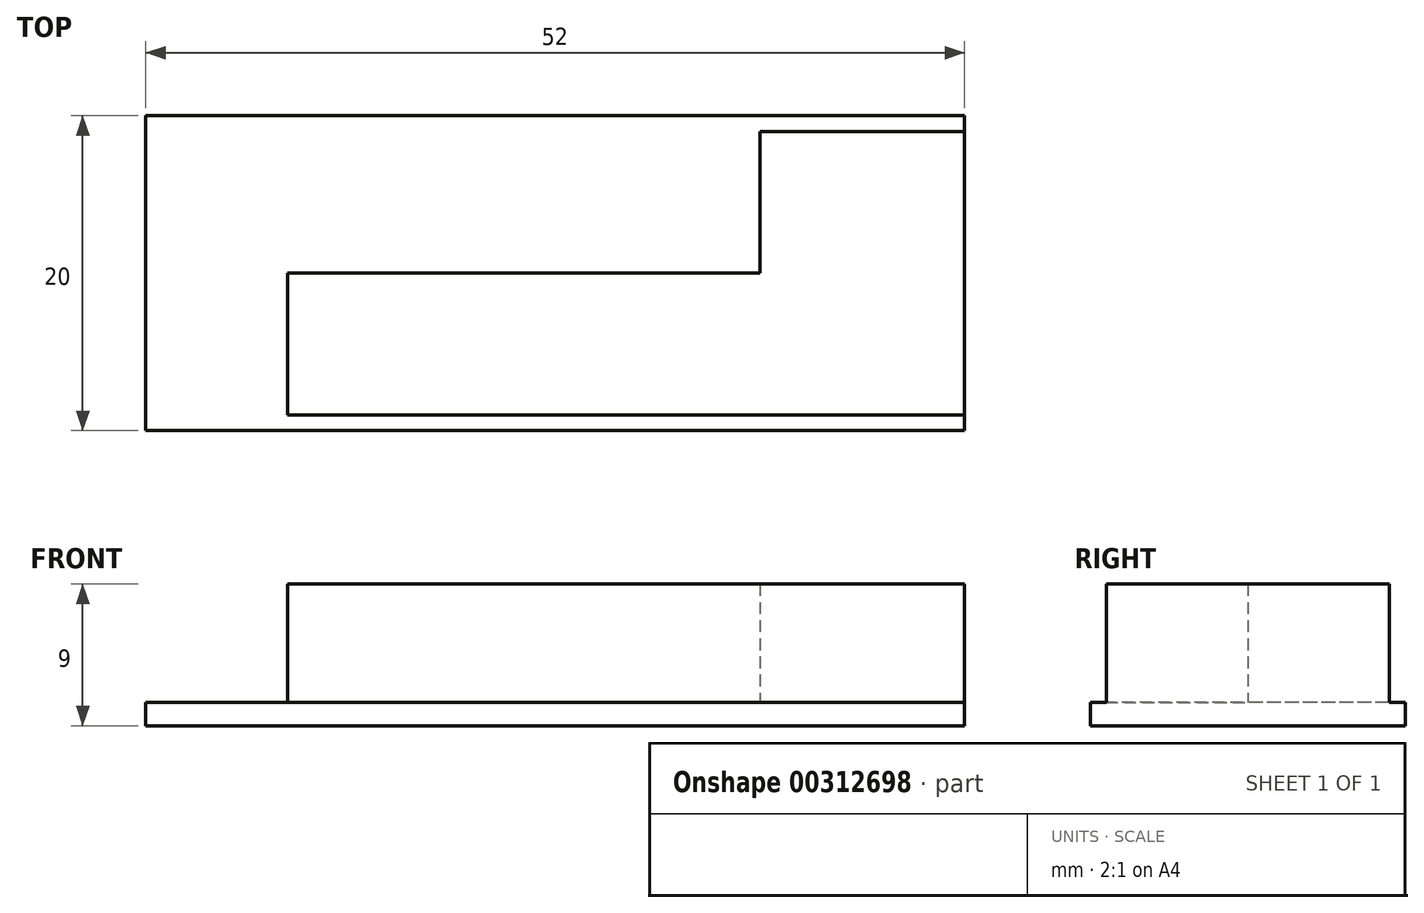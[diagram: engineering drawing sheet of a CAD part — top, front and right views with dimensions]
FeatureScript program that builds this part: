
annotation { "Feature Type Name" : "Feature", "Feature Type Description" : "" }
export const myFeature = defineFeature(function(context is Context, id is Id, definition is map)
    precondition{}
    {
        {
            var Q0;
            Q0=qCreatedBy(makeId("Top.planeOp"),FACE);
            var sketch = newSketch(context, id + "F0", { "sketchPlane" : qUnion([Q0])});
            skLineSegment(sketch, "E0.bottom", {"start": v(0, 0) * mm, "end": v(52, 0) * mm});
            skLineSegment(sketch, "E0.top", {"start": v(0, -20) * mm, "end": v(52, -20) * mm});
            skLineSegment(sketch, "E0.left", {"start": v(0, 0) * mm, "end": v(0, -20) * mm});
            skLineSegment(sketch, "E0.right", {"start": v(52, 0) * mm, "end": v(52, -20) * mm});
            skSolve(sketch);
        }
        {
            var Q0;
            Q0=makeQuery(id+"F0.imprint","IMPRINT",FACE,{"disambiguationData":[TD([[makeQuery(id+"F0.imprint","IMPRINT",EDGE,{"derivedFrom":sQuery(id+"F0.wireOp",EDGE,"E0.bottom")}),-1.0]])]});
            extrude(context, id + "F1", {"entities" : qUnion([Q0]), "depth" : 1.5 * mm});
        }
        {
            var Q0;
            Q0=makeQuery(id+"F1.opExtrude","CAP_FACE",FACE,{"disambiguationData":[OSD([sQuery(id+"F0.wireOp",EDGE,"E0.bottom"),sQuery(id+"F0.wireOp",EDGE,"E0.top"),sQuery(id+"F0.wireOp",EDGE,"E0.left"),sQuery(id+"F0.wireOp",EDGE,"E0.right")])],"isStart":false});
            var sketch = newSketch(context, id + "F2", { "sketchPlane" : qUnion([Q0])});
            skLineSegment(sketch, "E1.bottom", {"start": v(52, -1) * mm, "end": v(39, -1) * mm});
            skLineSegment(sketch, "E1.top", {"start": v(52, -19) * mm, "end": v(39, -19) * mm});
            skLineSegment(sketch, "E1.left", {"start": v(52, -1) * mm, "end": v(52, -19) * mm});
            skLineSegment(sketch, "E1.right", {"start": v(39, -1) * mm, "end": v(39, -19) * mm});
            skPoint(sketch, "E2.oppositeSnap0", {"position": v(39, -10) * mm});
            skLineSegment(sketch, "E2.bottom", {"start": v(39, -19) * mm, "end": v(9, -19) * mm});
            skLineSegment(sketch, "E2.top", {"start": v(39, -10) * mm, "end": v(9, -10) * mm});
            skLineSegment(sketch, "E2.left", {"start": v(39, -19) * mm, "end": v(39, -10) * mm});
            skLineSegment(sketch, "E2.right", {"start": v(9, -19) * mm, "end": v(9, -10) * mm});
            skSolve(sketch);
        }
        {
            var Q0;
            Q0=makeQuery(id+"F2.imprint","IMPRINT",FACE,{"disambiguationData":[TD([[makeQuery(id+"F2.imprint","IMPRINT",EDGE,{"derivedFrom":sQuery(id+"F2.wireOp",EDGE,"E2.bottom")}),-1.0]])]});
            var Q1;
            Q1=makeQuery(id+"F2.imprint","IMPRINT",FACE,{"disambiguationData":[TD([[makeQuery(id+"F2.imprint","IMPRINT",EDGE,{"derivedFrom":sQuery(id+"F2.wireOp",EDGE,"E1.bottom")}),1.0]])]});
            extrude(context, id + "F3", {"entities" : qUnion([Q0, Q1]), "operationType" : NewBodyOperationType.ADD, "depth" : (9 - 1.5) * mm});
        }
    });
